# Revit family: Chair-Multi-Purpose-Allermuir-Scoop-A430
name_source: partatom
category: Furniture
revit_build: Autodesk Revit Architecture 2012 (Build: 20110309_2315(x64)
units: mm (PartAtom-declared; Revit-internal decimal feet)

## types (1)
- A430
    04 CSI = 12 51 00
    2.5" Casters = No
    95 CSI = 12510
    Advanced Sync Tilt with Multi Position Back = No
    Airflow Back Mesh = No
    Assembly Code = E2020200
    Back = Stainless - Polished Brushed
    Base Type = 4 leg frame
    Base or Frame = Round Steel tube frame in Silver M04 EPPC
    Black Components = No
    Black GRP Base = No
    Black Gas Lift = No
    Black Plastic Back Membrane = No
    Brochure URL = http://www.allermuir.net
    CAD Blocks URL = http://www.allermuir.net
    Color Availability = See price list for material options
    Description = High stool
    Detachable writing table = No
    Fabric Spec Sheets = http://www.allermuir.net
    Glides = Coarse Textured - Black
    Height Adjustable Arms = No
    Height Adjustable Arms with Multi funtction Pad = No
    LEED Stats URL = http://www.allermuir.net
    Lumbar Adjustment = No
    Manufacturer = Allermuir
    Manufacturer Fax = (419) 887 5805
    Model = A430
    Negative Seat Tilt = No
    Optional Feature Notes = Beech shell can be stained, see page 011 for stain options,  Round Steel tube frame in Polished Chrome frame and Chrome frame, counter height stool option
    Overall Depth = 450 mm  [stored 1.47638 ft]
    Overall Height = 820 mm  [stored 2.69029 ft]
    Overall Width = 440 mm  [stored 1.44357 ft]
    Pedestal Base = NO
    Plastic Arms in Black = NO
    Plugin Data URL = http://products.ecoscorecard.com
    Polished Aluminum Arm Carrier = No
    Polished Aluminum Base = No
    Pricing URL = http://www.allermuir.net
    Product Line = Scoop
    Product Page URL = http://www.allermuir.net
    Seat Depth = 381 mm  [stored 1.25 ft]
    Seat Depth Adjustment = No
    Seat Height = 755 mm  [stored 2.47703 ft]
    Seat Width = 406 mm
    Seat or Base = Wood - Allermuir - Plywood - New
    Slimline Upholstery = No
    Specifications URL = http://www.allermuir.net
    Stacks = No
    Subcategory = Multi-Purpose Line
    Swaged Tubular Steel Legs = YES
    URL = http://www.allermuir.net
    Upholstered Back = NO
    Upholstered Seat = NO
    Weight = 16.0 lb
    ecoScorecard Product Page = http://products.ecoscorecard.com
    ecoScorecard_data = http://thesenatorgroup.ecoscorecard.com

note: [stored X ft] marks values corroborated as IEEE doubles in the binary element streams (Revit-internal decimal feet)

## geometry (parser evidence)
native form markers: Blend x11, Sweep x2
no freeform markers — native parametric forms only
